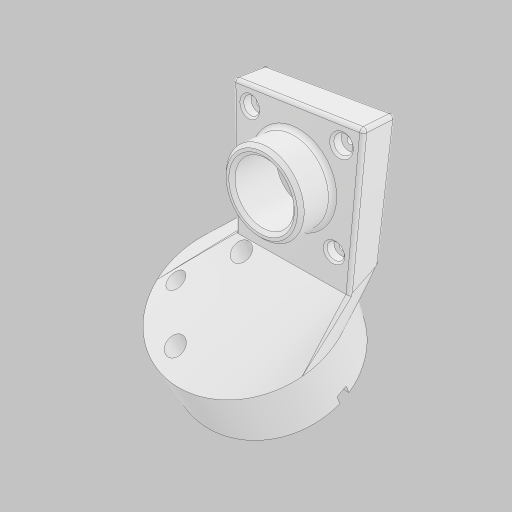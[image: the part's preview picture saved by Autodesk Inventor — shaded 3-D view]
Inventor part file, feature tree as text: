
AUTODESK INVENTOR PART (.ipt)
format: ipt  version: 2023.5 (Build 275446000, 446)  size: 772,608 bytes
history: native  units: in
note: dims shown in document units (in); Inventor stores cm internally (conversion verified against a paired STEP export)
features: extrude x11, projected_geometry x10, sketch x9, fillet x6, plane x3, hole x3, other x3, chamfer x2, thicken_offset x2, loft x1, sweep x1, revolve x1
ambient origin geometry x8: Origin, YZ Plane, XZ Plane, XY Plane, X Axis, Y Axis, Z Axis, Center Point
bodies: Solid1 (feature_tree)
feature tree (52):
  extrude  "Extrusion1"  Depth=0.525in
  extrude  "Extrusion2"  Depth=0.4673in
  plane  "Work Plane1"
  extrude  "Extrusion3"  Depth=0.6in
  loft  "Loft1"
  extrude  "Extrusion4"  TaperAngle=0.0deg  [1 undecoded]
  hole  "Hole1"  [1 undecoded]
  extrude  "Extrusion5"  Depth=0.0312in
  extrude  "Extrusion6"  Depth=0.0312in TaperAngle=0.0deg
  hole  "Hole2"  [1 undecoded]
  plane  "Work Plane2"
  fillet  "Fillet1"  Radius=1.3386in
  chamfer  "Chamfer1"  Distance=0.15in
  fillet  "Fillet2"  Radius=0.9792in
  extrude  "Extrusion7"  Depth=0.0312in
  fillet  "Fillet3"  [1 undecoded]
  chamfer  "Chamfer2"  Distance=0.05in
  thicken_offset  "Thicken1"
  hole  "Hole4"  [1 undecoded]
  extrude  "Extrusion8"  Depth=0.0312in
  sketch  "Sketch13"  dims[d5=1.875in d6=0.0in d7=0.6in]
  sketch  "3D Sketch1"
  extrude  "Extrusion9"  Depth=0.0312in
  extrude  "Extrusion10"  Depth=0.0312in TaperAngle=0.0deg
  sketch  "Sketch15"  dims[d12=0.0in d13=90.0deg d14=0.0in d15=90.0deg]
  plane  "Work Plane3"
  sketch  "Sketch16"  dims[d16=1.6in d17=0.3in d18=0.0in]
  sweep  "Sweep1"
  fillet  "Fillet6"  Radius=0.0312in
  thicken_offset  "Thicken2"
  fillet  "Fillet7"  Radius=0.2405in
  extrude  "Extrusion11"  TaperAngle=90.0deg  [1 undecoded]
  fillet  "Fillet9"  Radius=1.0in
  other  "Edges1"
  other  "Edges2"
  projected_geometry  "Projected Loop1"
  projected_geometry  "Projected Loop2"
  sketch  "Sketch11"  dims[d0=1.875in d1=0.525in]
  other  "Srf1"
  sketch  "Sketch12"  dims[d2=1.875in d3=0.0in d4=0.4673in]
  projected_geometry  "Projected Loop3"
  sketch  "Sketch14"  dims[d9=2.75in d10=0.1in d11=0.0in]
  projected_geometry  "Projected Loop4"
  sketch  "3D Sketch2"
  sketch  "Sketch17"  dims[d19=0.9in d20=0.75in d21=0.119in d22=0.25in d23=0.6871in d24=1.0in d25=0.8108in d26=1.1875in d27=0.5in d28=0.0in d29=0.1839in d30=1.3386in d31=0.15in d32=0.0in d33=0.094in d34=0.75in d35=0.251in d36=0.15in d37=0.6871in d38=1.0in d39=0.8108in d40=0.9792in d41=0.9792in d42=315.0deg d52=0.05in d53=0.05in d54=0.125in d55=45.0deg d56=0.0625in d57=1.0in d58=1.0in d59=0.0in d60=0.25in d61=0.0312in d62=0.125in d63=45.0deg d64=0.2405in d65=90.0deg d66=1.0in d67=1.0in d68=0.177in d69=0.75in d70=0.313in d71=1.45in d72=0.5635in d73=1.0in d74=0.8108in d75=1.25in d76=0.87in d77=1.0in d78=0.0in d79=0.1875in d80=1.5in d81=0.0in d82=0.1875in d83=0.25in d84=0.0in d85=0.1875in d86=0.1875in d87=0.0in d88=0.0in d92=0.0312in d93=0.1in d94=0.1in d95=0.0156in d97=0.1875in d98=0.1875in d99=0.1875in d100=0.1875in d101=0.0in d102=0.0312in]
  revolve  "RevolutionSrf1"  [1 undecoded]
  projected_geometry  "Project Cut Edges1"
  projected_geometry  "Project Cut Edges2"
  projected_geometry  "Project Cut Edges3"
  projected_geometry  "Project Cut Edges4"
  projected_geometry  "Project Cut Edges5"
  projected_geometry  "Project Cut Edges6"
note: 7 required parameter values undecoded (feature->parameter linkage not recoverable at this tier; creation-order binding heuristic only, values carry confidence <= 0.55)